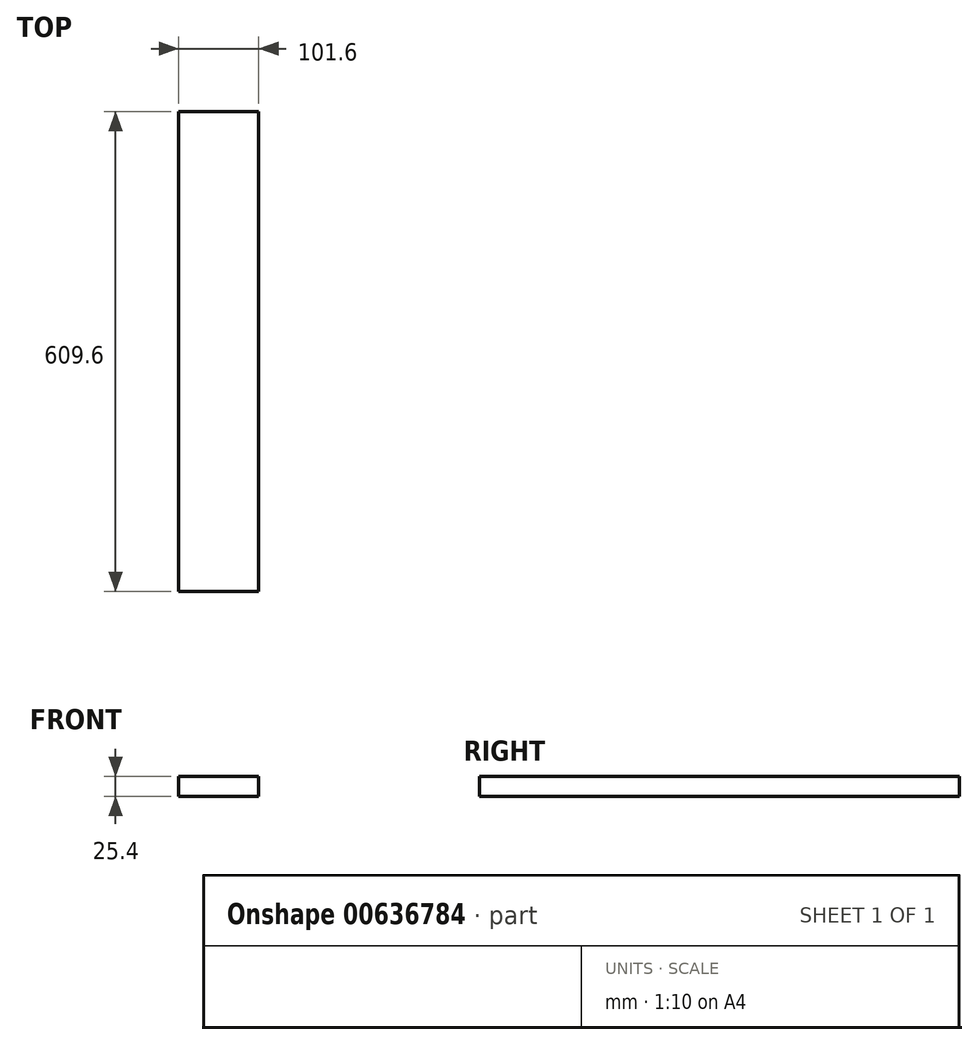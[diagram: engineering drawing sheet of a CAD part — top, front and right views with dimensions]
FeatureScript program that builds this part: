
annotation { "Feature Type Name" : "Feature", "Feature Type Description" : "" }
export const myFeature = defineFeature(function(context is Context, id is Id, definition is map)
    precondition{}
    {
        {
            var Q0;
            Q0=qCreatedBy(makeId("Top.planeOp"),FACE);
            var sketch = newSketch(context, id + "F0", { "sketchPlane" : qUnion([Q0])});
            skLineSegment(sketch, "E0.bottom", {"start": v(-50.8, 304.8) * mm, "end": v(50.8, 304.8) * mm});
            skLineSegment(sketch, "E0.top", {"start": v(-50.8, -304.8) * mm, "end": v(50.8, -304.8) * mm});
            skLineSegment(sketch, "E0.left", {"start": v(-50.8, 304.8) * mm, "end": v(-50.8, -304.8) * mm});
            skLineSegment(sketch, "E0.right", {"start": v(50.8, 304.8) * mm, "end": v(50.8, -304.8) * mm});
            skSolve(sketch);
        }
        {
            var Q0;
            Q0 = qSketchRegion(id + "F0", true);
            extrude(context, id + "F1", {"entities" : qUnion([Q0]), "depth" : 25.4 * mm, "offsetDistance" : 25 * mm});
        }
    });
